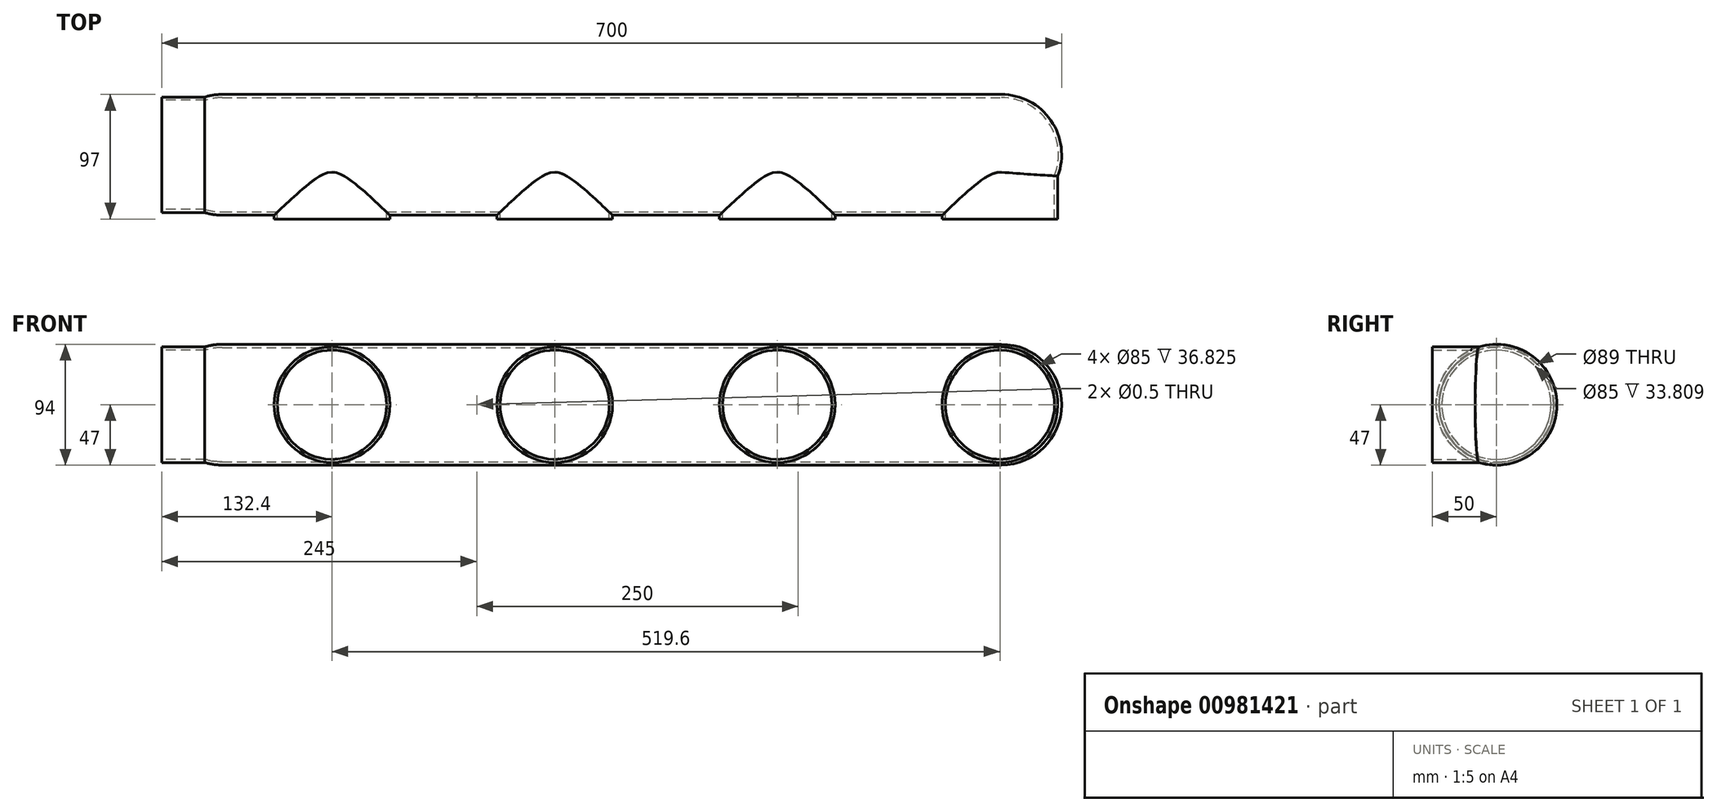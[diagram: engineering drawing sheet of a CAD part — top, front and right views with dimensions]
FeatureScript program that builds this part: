
annotation { "Feature Type Name" : "Feature", "Feature Type Description" : "" }
export const myFeature = defineFeature(function(context is Context, id is Id, definition is map)
    precondition{}
    {
        {
            var Q0;
            Q0=qCreatedBy(makeId("Front.planeOp"),FACE);
            var sketch = newSketch(context, id + "F0", { "sketchPlane" : qUnion([Q0])});
            skLineSegment(sketch, "E0.bottom", {"start": v(-350, 47) * mm, "end": v(350, 47) * mm});
            skLineSegment(sketch, "E0.top", {"start": v(-350, -47) * mm, "end": v(350, -47) * mm});
            skLineSegment(sketch, "E0.left", {"start": v(-350, 47) * mm, "end": v(-350, -47) * mm});
            skLineSegment(sketch, "E0.right", {"start": v(350, 47) * mm, "end": v(350, -47) * mm});
            skPoint(sketch, "E0.middle", {"position": v(0, 0) * mm});
            skSolve(sketch);
        }
        {
            var Q0;
            Q0=makeQuery(id+"F0.imprint","IMPRINT",FACE,{"disambiguationData":[TD([[makeQuery(id+"F0.imprint","IMPRINT",EDGE,{"derivedFrom":sQuery(id+"F0.wireOp",EDGE,"E0.bottom")}),-1.0]])]});
            extrude(context, id + "F1", {"entities" : qUnion([Q0]), "endBound" : BoundingType.SYMMETRIC, "depth" : 94 * mm, "offsetDistance" : 25 * mm});
        }
        {
            var Q0;
            Q0=makeQuery(id+"F1.opExtrude","SWEPT_FACE",FACE,{"disambiguationData":[OSD([sQuery(id+"F0.wireOp",EDGE,"E0.left")])]});
            cPlane(context, id + "F2", {"entities" : qUnion([Q0]), "cplaneType" : CPlaneType.OFFSET, "offset" : 0 * mm, "width" : 150 * mm, "height" : 150 * mm});
        }
        {
            var Q0;
            Q0=makeQuery(id+"F1.opExtrude","SWEPT_FACE",FACE,{"disambiguationData":[OSD([sQuery(id+"F0.wireOp",EDGE,"E0.bottom")])]});
            var Q1;
            Q1=makeQuery(id+"F1.opExtrude","CAP_FACE",FACE,{"disambiguationData":[OSD([sQuery(id+"F0.wireOp",EDGE,"E0.bottom"),sQuery(id+"F0.wireOp",EDGE,"E0.top"),sQuery(id+"F0.wireOp",EDGE,"E0.left"),sQuery(id+"F0.wireOp",EDGE,"E0.right")])],"isStart":false});
            var Q2;
            Q2=makeQuery(id+"F1.opExtrude","SWEPT_FACE",FACE,{"disambiguationData":[OSD([sQuery(id+"F0.wireOp",EDGE,"E0.top")])]});
            var Q3;
            Q3=makeQuery(id+"F1.opExtrude","CAP_FACE",FACE,{"disambiguationData":[OSD([sQuery(id+"F0.wireOp",EDGE,"E0.bottom"),sQuery(id+"F0.wireOp",EDGE,"E0.top"),sQuery(id+"F0.wireOp",EDGE,"E0.left"),sQuery(id+"F0.wireOp",EDGE,"E0.right")])],"isStart":true});
            var Q4;
            Q4=makeQuery(id+"F1.opExtrude","SWEPT_FACE",FACE,{"disambiguationData":[OSD([sQuery(id+"F0.wireOp",EDGE,"E0.right")])]});
            fillet(context, id + "F3", {"entities" : qUnion([Q0, Q1, Q2, Q3, Q4]), "radius" : 47 * mm, "tangentPropagation" : true, "allowEdgeOverflow" : false});
        }
        {
            var Q0;
            Q0=qCreatedBy(id+"F2.planeOp",FACE);
            var sketch = newSketch(context, id + "F4", { "sketchPlane" : qUnion([Q0])});
            skCircle(sketch, "E1", {"center": v(0, 0) * mm, "radius": 45 * mm});
            skSolve(sketch);
        }
        {
            var Q0;
            Q0=qSketchRegion(id+"F4",true);
            extrude(context, id + "F5", {"entities" : qUnion([Q0]), "operationType" : NewBodyOperationType.ADD, "oppositeDirection" : true, "depth" : 100 * mm, "offsetDistance" : 25 * mm});
        }
        {
            var Q0;
            Q0=qCreatedBy(makeId("Front.planeOp"),FACE);
            var sketch = newSketch(context, id + "F6", { "sketchPlane" : qUnion([Q0])});
            skCircle(sketch, "E2", {"center": v(-44.4, 0) * mm, "radius": 45 * mm});
            skCircle(sketch, "E3", {"center": v(128.8, 0) * mm, "radius": 45 * mm});
            skCircle(sketch, "E4", {"center": v(302, 0) * mm, "radius": 45 * mm});
            skCircle(sketch, "E5", {"center": v(-217.6, 0) * mm, "radius": 45 * mm});
            skSolve(sketch);
        }
        {
            var Q0;
            Q0=qSketchRegion(id+"F6",true);
            extrude(context, id + "F7", {"entities" : qUnion([Q0]), "operationType" : NewBodyOperationType.ADD, "depth" : 50 * mm, "offsetDistance" : 25 * mm});
        }
        {
            var Q0;
            Q0=makeQuery(id+"F7.opExtrude","CAP_FACE",FACE,{"disambiguationData":[OSD([sQuery(id+"F6.wireOp",EDGE,"21sKYaGF-B368-Wwl2-OhkZ-wf8vG0b8O0Hr")])],"isStart":false});
            var Q1;
            Q1=makeQuery(id+"F7.opExtrude","CAP_FACE",FACE,{"disambiguationData":[OSD([sQuery(id+"F6.wireOp",EDGE,"aba59EDD-dIZK-h3VM-gZ2g-2MMW7iUeaAD7")])],"isStart":false});
            var Q2;
            Q2=makeQuery(id+"F7.opExtrude","CAP_FACE",FACE,{"disambiguationData":[OSD([sQuery(id+"F6.wireOp",EDGE,"uwOiRNa3-sxhi-IzUB-w2N1-3xDbzfmg6dx9")])],"isStart":false});
            var Q3;
            Q3=makeQuery(id+"F7.opExtrude","CAP_FACE",FACE,{"disambiguationData":[OSD([sQuery(id+"F6.wireOp",EDGE,"E5")])],"isStart":false});
            var Q4;
            Q4=makeQuery(id+"F7.opExtrude","CAP_FACE",FACE,{"disambiguationData":[OSD([sQuery(id+"F6.wireOp",EDGE,"E2")])],"isStart":false});
            var Q5;
            Q5=makeQuery(id+"F7.opExtrude","CAP_FACE",FACE,{"disambiguationData":[OSD([sQuery(id+"F6.wireOp",EDGE,"E3")])],"isStart":false});
            var Q6;
            Q6=makeQuery(id+"F7.opExtrude","CAP_FACE",FACE,{"disambiguationData":[OSD([sQuery(id+"F6.wireOp",EDGE,"E4")])],"isStart":false});
            var Q7;
            Q7=makeQuery(id+"F5.opExtrude","CAP_FACE",FACE,{"disambiguationData":[OSD([sQuery(id+"F4.wireOp",EDGE,"E1")])],"isStart":true});
            shell(context, id + "F8", {"entities" : qUnion([Q0, Q1, Q2, Q3, Q4, Q5, Q6, Q7]), "thickness" : 2.5 * mm});
        }
        {
            var Q0;
            Q0=qCreatedBy(makeId("Front.planeOp"),FACE);
            cPlane(context, id + "F9", {"entities" : qUnion([Q0]), "cplaneType" : CPlaneType.OFFSET, "offset" : 47 * mm, "oppositeDirection" : true, "width" : 150 * mm, "height" : 150 * mm});
        }
        {
            var Q0;
            Q0=qCreatedBy(id+"F9.planeOp",FACE);
            var sketch = newSketch(context, id + "F10", { "sketchPlane" : qUnion([Q0])});
            skPoint(sketch, "E6", {"position": v(145, 0) * mm});
            skPoint(sketch, "E7", {"position": v(-105, 0) * mm});
            skSolve(sketch);
        }
        {
            var Q0;
            Q0=sQuery(id+"F10.wireOp",VERTEX,"E6");
            var Q1;
            Q1=sQuery(id+"F10.wireOp",VERTEX,"E7");
            var Q2;
            Q2=makeQuery(id+"F1.opExtrude","SWEPT_BODY",BODY,{"disambiguationData":[OSD([sQuery(id+"F0.wireOp",EDGE,"E0.bottom"),sQuery(id+"F0.wireOp",EDGE,"E0.top"),sQuery(id+"F0.wireOp",EDGE,"E0.left"),sQuery(id+"F0.wireOp",EDGE,"E0.right")])]});
            hole(context, id + "F11", {"style" : HoleStyle.SIMPLE, "endStyle" : HoleEndStyle.BLIND, "oppositeDirection" : true, "holeDiameter" : 0.5 * mm, "majorDiameter" : 5 * mm, "holeDepth" : 50 * mm, "isTappedThrough" : true, "tappedDepth" : 12 * mm, "tapClearance" : 3, "startFromSketch" : true, "locations" : qUnion([Q0, Q1]), "scope" : qUnion([Q2])});
        }
    });
